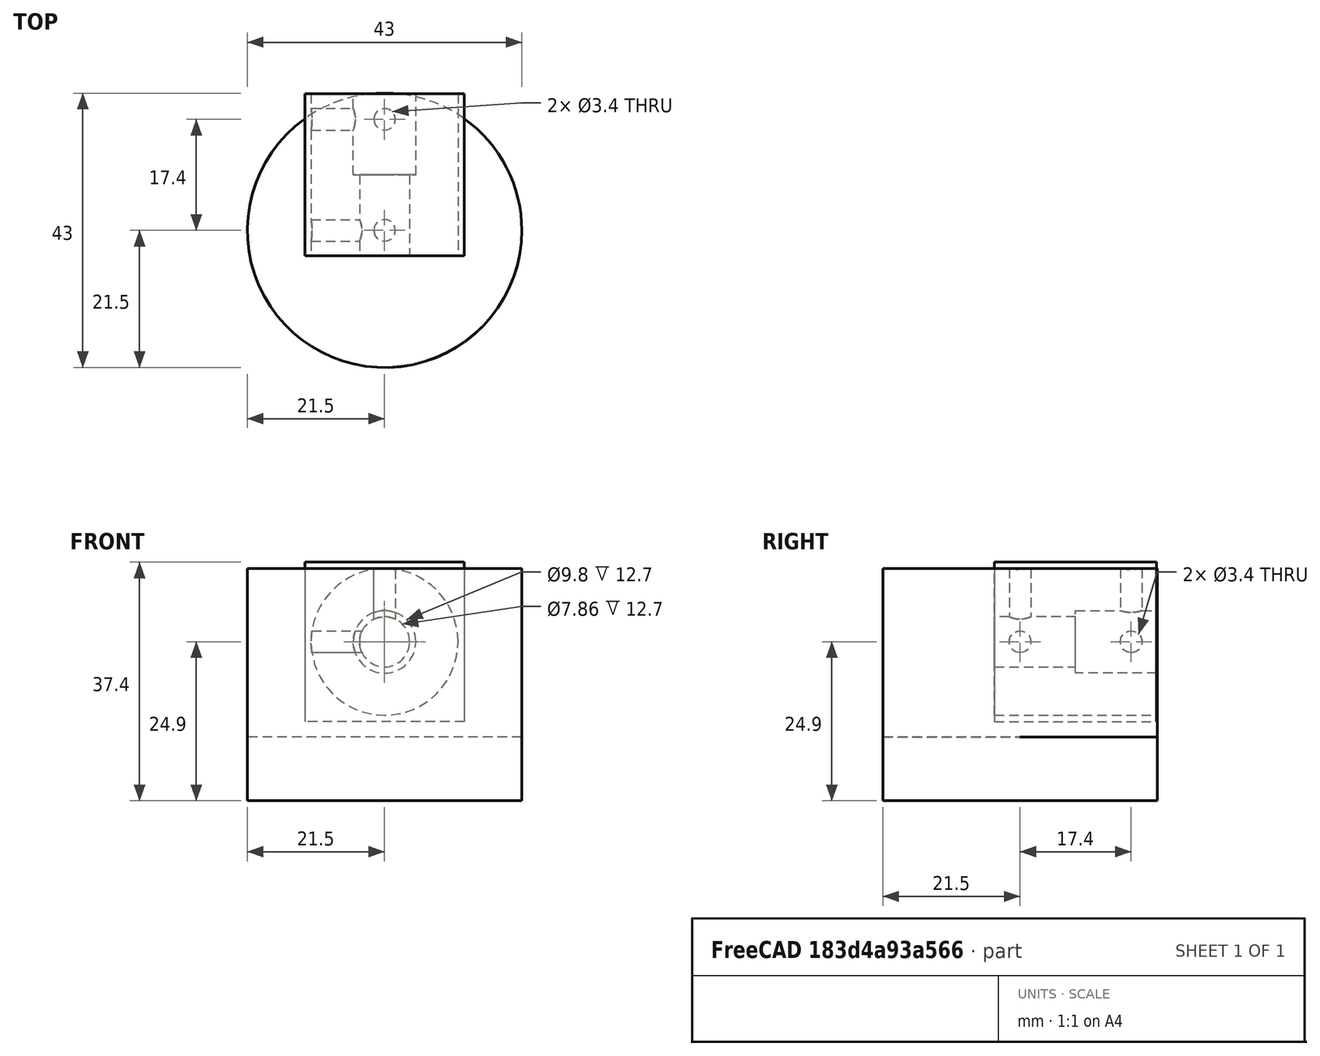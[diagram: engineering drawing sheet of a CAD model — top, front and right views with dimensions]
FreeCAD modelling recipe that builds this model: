
FCSTD DOCUMENT  (FreeCAD 0.17R13320 (Git))
Label: motor_coupler
License: All rights reserved
LicenseURL: http://en.wikipedia.org/wiki/All_rights_reserved
objects: Path::FeaturePython×15, Part::FeaturePython×6, Sketcher::SketchObject×4, PartDesign::Pocket×3, App::FeaturePython×3, Path::FeatureCompoundPython×3, PartDesign::Pad×1, PartDesign::Body×1, Mesh::FeaturePython×1
note: 22 computed .brp shape members not serialized (recipe doc carries the construction recipe); baked Part::Feature solids carry a one-line shape summary decoded from their .brp

FEATURE [Sketcher::SketchObject] Sketch
  MapMode = 5
  Support = -> [XY_Plane]
  sketch-geometry (2):
    g0: Circle CenterX=0 CenterY=0 CenterZ=0 NormalX=0 NormalY=0 NormalZ=1 AngleXU=0 Radius=11.5
    g1: Circle CenterX=0 CenterY=0 CenterZ=0 NormalX=0 NormalY=0 NormalZ=1 AngleXU=0 Radius=3.93
  constraints (4):
    c: Coincident(g0,g-1)
    c: Coincident(g1,g-1)
    c: Radius(g0) = 11.5
    c: Radius(g1) = 3.93
FEATURE [PartDesign::Pad] Pad
  Length = 25.4
  Length2 = 100
  Profile = -> Sketch
  Type = 0
FEATURE [Sketcher::SketchObject] Sketch001
  MapMode = 5
  Placement = pos=(0,0,25.4) rot=(0,0,1;0rad)
  Support = -> [Pad]
  sketch-geometry (1):
    g0: Circle CenterX=0 CenterY=0 CenterZ=0 NormalX=0 NormalY=0 NormalZ=1 AngleXU=0 Radius=4.9
  constraints (2):
    c: Radius(g0) = 4.9
    c: Coincident(g0,g-1)
FEATURE [PartDesign::Pocket] Pocket
  BaseFeature = -> Pad
  Length = 12.7
  Length2 = 100
  Profile = -> Sketch001
  Type = 0
FEATURE [Sketcher::SketchObject] Sketch002
  MapMode = 5
  Placement = pos=(0,0,0) rot=(1,0,0;1.5708rad)
  Support = -> [XZ_Plane]
  sketch-geometry (2):
    g0: Circle CenterX=0 CenterY=4 CenterZ=0 NormalX=0 NormalY=0 NormalZ=1 AngleXU=0 Radius=1.7
    g1: Circle CenterX=0 CenterY=21.4 CenterZ=0 NormalX=0 NormalY=0 NormalZ=1 AngleXU=0 Radius=1.7
  constraints (6):
    c: DistanceX(g-1,g0) = 0
    c: DistanceX(g-1,g1) = 0
    c: DistanceY(g-1,g0) = 4
    c: DistanceY(g-1,g1) = 21.4
    c: Radius(g0) = 1.7
    c: Equal(g1,g0)
FEATURE [PartDesign::Pocket] Pocket001
  BaseFeature = -> Pocket
  Length = 5
  Length2 = 100
  Profile = -> Sketch002
  Type = 1
FEATURE [Sketcher::SketchObject] Sketch003
  MapMode = 5
  Placement = pos=(0,0,0) rot=(0.57735,0.57735,0.57735;2.0944rad)
  Support = -> [YZ_Plane]
  sketch-geometry (2):
    g0: Circle CenterX=0 CenterY=4 CenterZ=0 NormalX=0 NormalY=0 NormalZ=1 AngleXU=0 Radius=1.7
    g1: Circle CenterX=0 CenterY=21.4 CenterZ=0 NormalX=0 NormalY=0 NormalZ=1 AngleXU=0 Radius=1.7
  constraints (6):
    c: PointOnObject(g0,g-2)
    c: PointOnObject(g1,g-2)
    c: DistanceY(g-1,g0) = 4
    c: DistanceY(g-1,g1) = 21.4
    c: Radius(g0) = 1.7
    c: Equal(g0,g1)
FEATURE [PartDesign::Pocket] Pocket002
  BaseFeature = -> Pocket001
  Length = 5
  Length2 = 100
  Profile = -> Sketch003
  Type = 1
FEATURE [PartDesign::Body] Body
  Group = -> [Sketch,Pad,Sketch001,Pocket,Sketch002,Pocket001,Sketch003,Pocket002]
  Origin = -> Origin
  Tip = -> Pocket002
FEATURE [App::FeaturePython] SetupSheet  # Path/CAM operation (typed FeaturePython)
  ClearanceHeightExpression = StartDepth+SetupSheet.ClearanceHeightOffset
  ClearanceHeightOffset = 5
  FinalDepthExpression = OpFinalDepth
  HorizRapid = 0
  SafeHeightExpression = StartDepth+SetupSheet.SafeHeightOffset
  SafeHeightOffset = 3
  StartDepthExpression = OpStartDepth
  StepDownExpression = OpToolDiameter
  VertRapid = 0
FEATURE [Part::FeaturePython] Clone  label="Base-Body"  # Draft clone (typed FeaturePython)
  AttacherType = Attacher::AttachEngine3D
  Fuse = false
  Objects = -> [Body]
  PathResource = Base
  Placement = pos=(0,0,-26.4) rot=(0,0,1;0rad)
  Scale = (1,1,1)
FEATURE [Path::FeaturePython] Default_Tool  label="Default Tool"  # Path/CAM operation (typed FeaturePython)
  HorizFeed = 0
  HorizRapid = 0
  SpindleDir = 0
  SpindleSpeed = 0
  ToolNumber = 1
  VertFeed = 0
  VertRapid = 0
  expr: HorizRapid = SetupSheet.HorizRapid
  expr: VertRapid = SetupSheet.VertRapid
FEATURE [Part::FeaturePython] Stock001  # WARN: FeaturePython — macro-defined, semantics opaque (R4)
  Height = 26.4
  Placement = pos=(0,0.0031811,-26.4) rot=(0,0,1;0rad)
  Radius = 21.5
  StockType = CreateCylinder
FEATURE [Path::FeaturePython] T3__8mm  label="T3: 8mm"  # Path/CAM operation (typed FeaturePython)
  HorizFeed = 0
  HorizRapid = 0
  SpindleDir = 0
  SpindleSpeed = 0
  ToolNumber = 3
  VertFeed = 0
  VertRapid = 0
  expr: HorizRapid = SetupSheet.HorizRapid
  expr: VertRapid = SetupSheet.VertRapid
FEATURE [Path::FeaturePython] MillFace  # Path/CAM operation (typed FeaturePython)
  Active = true
  AreaParams:
    OpenMode = 0
    Angle = 45.0
    MinArcPoints = 4
    Coplanar = 0
    Tolerance = 1e-07
    CleanDistance = 0.0
    PocketExtraOffset = -1.0
    RoundPrecision = 0.0
    AngleShift = 0.0
    SubjectFill = 0
    PocketMode = 2
    Simplify = False
    SectionTolerance = 1e-06
    MaxArcPoints = 100
    Offset = 0.0
    Accuracy = 0.01
    PocketStepover = 3.2
    ClipFill = 0
    ToolRadius = 4.0
    Outline = False
    ClipperScale = 10000000.0
    FromCenter = True
    Explode = False
    EndType = 0
    Shift = 0.0
    ExtraPass = 0
    Project = False
    JoinType = 0
    Thicken = False
    Stepdown = 1.0
    SectionMode = 2
    MiterLimit = 2.0
    Deflection = 0.01
    Reorient = True
    FitArcs = True
    SectionCount = -1
    SectionOffset = 0.0
    Stepover = 0.0
    Unit = 1.0
    Fill = 0
  Base = -> [Clone]
  BoundaryShape = 0
  ClearanceHeight = 5
  CutMode = 0
  ExtraOffset = 1
  FinalDepth = -1
  FinishDepth = 0
  KeepToolDown = false
  MinTravel = false
  OffsetPattern = 1
  OpFinalDepth = -1
  OpStartDepth = 0
  OpToolDiameter = 8
  PathParams = {'resume_height': 3.0, 'feedrate': 0.0, 'verbose': True, 'orientation': 1, 'return_end': True, 'preamble': False, 'retraction': 5.0, 'feedrate_v': 0.0}
  SafeHeight = 3
  StartAt = 0
  StartDepth = 0
  StartPoint = (0,0,0)
  StepDown = 0.5
  StepOver = 40
  ToolController = -> T3__8mm
  UseStartPoint = false
  ZigZagAngle = 45
  expr: ClearanceHeight = StartDepth + SetupSheet.ClearanceHeightOffset
  expr: SafeHeight = StartDepth + SetupSheet.SafeHeightOffset
  expr: FinalDepth = OpFinalDepth
  expr: StartDepth = OpStartDepth
FEATURE [Path::FeaturePython] Helix  # Path/CAM operation (typed FeaturePython)
  Active = true
  Base = -> [Clone]
  ClearanceHeight = 5
  Direction = 0
  FinalDepth = -13.7
  OpFinalDepth = -13.7
  OpStartDepth = 0
  OpToolDiameter = 8
  SafeHeight = 3
  StartDepth = 0
  StartSide = 0
  StepDown = 0.5
  StepOver = 90
  ToolController = -> T3__8mm
  expr: ClearanceHeight = StartDepth + SetupSheet.ClearanceHeightOffset
  expr: SafeHeight = StartDepth + SetupSheet.SafeHeightOffset
  expr: FinalDepth = OpFinalDepth
  expr: StartDepth = OpStartDepth
FEATURE [Path::FeaturePython] Helix001  # Path/CAM operation (typed FeaturePython)
  Active = true
  Base = -> [Clone]
  ClearanceHeight = 5
  Direction = 0
  FinalDepth = -26.4
  OpFinalDepth = -26.4
  OpStartDepth = 0
  OpToolDiameter = 8
  SafeHeight = 3
  StartDepth = 0
  StartSide = 0
  StepDown = 1
  StepOver = 30
  ToolController = -> T3__8mm
  expr: ClearanceHeight = StartDepth + SetupSheet.ClearanceHeightOffset
  expr: SafeHeight = StartDepth + SetupSheet.SafeHeightOffset
  expr: FinalDepth = OpFinalDepth
  expr: StartDepth = OpStartDepth
FEATURE [Path::FeaturePython] Contour  # Path/CAM operation (typed FeaturePython)
  Active = true
  AreaParams:
    OpenMode = 0
    Angle = 45.0
    MinArcPoints = 4
    Coplanar = 2
    Tolerance = 1e-07
    CleanDistance = 0.0
    PocketExtraOffset = 0.0
    RoundPrecision = 0.0
    AngleShift = 0.0
    SubjectFill = 0
    PocketMode = 0
    Simplify = False
    SectionTolerance = 1e-06
    MaxArcPoints = 100
    Offset = 4.0
    Accuracy = 0.01
    PocketStepover = 0.0
    ClipFill = 0
    ToolRadius = 1.0
    Outline = False
    ClipperScale = 10000000.0
    FromCenter = False
    Explode = False
    EndType = 0
    Shift = 0.0
    ExtraPass = 0
    Project = False
    JoinType = 0
    Thicken = False
    Stepdown = 1.0
    SectionMode = 2
    MiterLimit = 2.0
    Deflection = 0.01
    Reorient = True
    FitArcs = True
    SectionCount = -1
    SectionOffset = 0.0
    Stepover = 0.0
    Unit = 1.0
    Fill = 0
  ClearanceHeight = 5
  Direction = 1
  FinalDepth = -26.4
  JoinType = 0
  MiterLimit = 0.1
  OffsetExtra = 0
  OpFinalDepth = -26.4
  OpStartDepth = 0
  OpToolDiameter = 8
  PathParams = {'resume_height': 3.0, 'feedrate': 0.0, 'verbose': True, 'orientation': 0, 'return_end': True, 'preamble': False, 'retraction': 5.0, 'feedrate_v': 0.0}
  SafeHeight = 3
  Side = 0
  StartDepth = 0
  StartPoint = (0,0,0)
  StepDown = 0.5
  ToolController = -> T3__8mm
  UseComp = true
  UseStartPoint = false
  expr: ClearanceHeight = StartDepth + SetupSheet.ClearanceHeightOffset
  expr: SafeHeight = StartDepth + SetupSheet.SafeHeightOffset
  expr: StartDepth = OpStartDepth
FEATURE [Path::FeatureCompoundPython] Operations  # Path/CAM operation (typed FeaturePython)
  Group = -> [MillFace,Helix,Helix001,Contour]
  UsePlacements = false
FEATURE [Path::FeaturePython] Job  # Path/CAM operation (typed FeaturePython)
  Base = -> Clone
  GeometryTolerance = 0.01
  Operations = -> Operations
  PostProcessor = 5
  SetupSheet = -> SetupSheet
  Stock = -> Stock001
  ToolController = -> [Default_Tool,T3__8mm]
FEATURE [Mesh::FeaturePython] CutMaterial  # WARN: FeaturePython — macro-defined, semantics opaque (R4)
FEATURE [App::FeaturePython] SetupSheet001  # Path/CAM operation (typed FeaturePython)
  ClearanceHeightExpression = StartDepth+SetupSheet001.ClearanceHeightOffset
  ClearanceHeightOffset = 5
  FinalDepthExpression = OpFinalDepth
  HorizRapid = 0
  SafeHeightExpression = StartDepth+SetupSheet001.SafeHeightOffset
  SafeHeightOffset = 3
  StartDepthExpression = OpStartDepth
  StepDownExpression = OpToolDiameter
  VertRapid = 0
FEATURE [Part::FeaturePython] Clone001  label="Base-Body001"  # Draft clone (typed FeaturePython)
  AttacherType = Attacher::AttachEngine3D
  Fuse = false
  Objects = -> [Body]
  PathResource = Base
  Placement = pos=(0,0,-11) rot=(1,0,0;3.14159rad)
  Scale = (1,1,1)
FEATURE [Path::FeaturePython] Default_Tool001  label="Default Tool001"  # Path/CAM operation (typed FeaturePython)
  HorizFeed = 0
  HorizRapid = 0
  SpindleDir = 0
  SpindleSpeed = 0
  ToolNumber = 1
  VertFeed = 0
  VertRapid = 0
  expr: HorizRapid = SetupSheet001.HorizRapid
  expr: VertRapid = SetupSheet001.VertRapid
FEATURE [App::FeaturePython] SetupSheet002  # Path/CAM operation (typed FeaturePython)
  ClearanceHeightExpression = StartDepth+SetupSheet002.ClearanceHeightOffset
  ClearanceHeightOffset = 5
  FinalDepthExpression = OpFinalDepth
  HorizRapid = 0
  SafeHeightExpression = StartDepth+SetupSheet002.SafeHeightOffset
  SafeHeightOffset = 3
  StartDepthExpression = OpStartDepth
  StepDownExpression = OpToolDiameter
  VertRapid = 0
FEATURE [Part::FeaturePython] Clone002  label="Base-Body002"  # Draft clone (typed FeaturePython)
  AttacherType = Attacher::AttachEngine3D
  Fuse = false
  Objects = -> [Body]
  PathResource = Base
  Placement = pos=(0,-4,-11.5) rot=(0.57735,-0.57735,-0.57735;4.18879rad)
  Scale = (1,1,1)
FEATURE [Path::FeaturePython] Default_Tool002  label="Default Tool002"  # Path/CAM operation (typed FeaturePython)
  HorizFeed = 0
  HorizRapid = 0
  SpindleDir = 0
  SpindleSpeed = 0
  ToolNumber = 1
  VertFeed = 0
  VertRapid = 0
  expr: HorizRapid = SetupSheet002.HorizRapid
  expr: VertRapid = SetupSheet002.VertRapid
FEATURE [Part::FeaturePython] Stock  # WARN: FeaturePython — macro-defined, semantics opaque (R4)
  Base = -> Body
  ExtXneg = 1
  ExtXpos = 1
  ExtYneg = 1
  ExtYpos = 1
  ExtZneg = 0
  ExtZpos = 0
  Placement = pos=(0,-4,-11.5) rot=(-0.57735,0.57735,0.57735;2.0944rad)
  StockType = FromBase
FEATURE [Path::FeaturePython] T8__3mm  label="T8: 3mm"  # Path/CAM operation (typed FeaturePython)
  HorizFeed = 0
  HorizRapid = 0
  SpindleDir = 0
  SpindleSpeed = 0
  ToolNumber = 8
  VertFeed = 0
  VertRapid = 0
  expr: HorizRapid = SetupSheet002.HorizRapid
  expr: VertRapid = SetupSheet002.VertRapid
FEATURE [Path::FeaturePython] Helix002  # Path/CAM operation (typed FeaturePython)
  Active = true
  Base = -> [Clone002]
  ClearanceHeight = 6
  Direction = 0
  FinalDepth = -7.71
  OpFinalDepth = -6.91251
  OpStartDepth = 1
  OpToolDiameter = 3
  SafeHeight = 4
  StartDepth = 1
  StartSide = 0
  StepDown = 0.5
  StepOver = 40
  ToolController = -> T8__3mm
  expr: ClearanceHeight = StartDepth + SetupSheet002.ClearanceHeightOffset
  expr: SafeHeight = StartDepth + SetupSheet002.SafeHeightOffset
  expr: StartDepth = OpStartDepth
FEATURE [Path::FeatureCompoundPython] Operations002  # Path/CAM operation (typed FeaturePython)
  Group = -> [Helix002]
  UsePlacements = false
FEATURE [Path::FeaturePython] Job002  # Path/CAM operation (typed FeaturePython)
  Base = -> Clone002
  GeometryTolerance = 0.01
  Operations = -> Operations002
  PostProcessor = 5
  SetupSheet = -> SetupSheet002
  Stock = -> Stock
  ToolController = -> [Default_Tool002,T8__3mm]
FEATURE [Path::FeaturePython] T3__8mm001  label="T3: 8mm001"  # Path/CAM operation (typed FeaturePython)
  HorizFeed = 0
  HorizRapid = 0
  SpindleDir = 0
  SpindleSpeed = 0
  ToolNumber = 3
  VertFeed = 0
  VertRapid = 0
  expr: HorizRapid = SetupSheet001.HorizRapid
  expr: VertRapid = SetupSheet001.VertRapid
FEATURE [Path::FeaturePython] MillFace001  # Path/CAM operation (typed FeaturePython)
  Active = true
  AreaParams:
    OpenMode = 0
    Angle = 45.0
    MinArcPoints = 4
    Coplanar = 0
    Tolerance = 1e-07
    CleanDistance = 0.0
    PocketExtraOffset = 2.0
    RoundPrecision = 0.0
    AngleShift = 0.0
    SubjectFill = 0
    PocketMode = 2
    Simplify = False
    SectionTolerance = 1e-06
    MaxArcPoints = 100
    Offset = 0.0
    Accuracy = 0.01
    PocketStepover = 3.2
    ClipFill = 0
    ToolRadius = 4.0
    Outline = False
    ClipperScale = 10000000.0
    FromCenter = True
    Explode = False
    EndType = 0
    Shift = 0.0
    ExtraPass = 0
    Project = False
    JoinType = 0
    Thicken = False
    Stepdown = 1.0
    SectionMode = 2
    MiterLimit = 2.0
    Deflection = 0.01
    Reorient = True
    FitArcs = True
    SectionCount = -1
    SectionOffset = 0.0
    Stepover = 0.0
    Unit = 1.0
    Fill = 0
  Base = -> [Clone001]
  BoundaryShape = 2
  ClearanceHeight = 5
  CutMode = 0
  ExtraOffset = -2
  FinalDepth = -11
  FinishDepth = 0
  KeepToolDown = false
  MinTravel = false
  OffsetPattern = 1
  OpFinalDepth = -11
  OpStartDepth = 0
  OpToolDiameter = 8
  PathParams = {'resume_height': 3.0, 'feedrate': 0.0, 'verbose': True, 'orientation': 1, 'return_end': True, 'preamble': False, 'retraction': 5.0, 'feedrate_v': 0.0}
  SafeHeight = 3
  StartAt = 0
  StartDepth = 0
  StartPoint = (0,0,0)
  StepDown = 0.5
  StepOver = 40
  ToolController = -> T3__8mm001
  UseStartPoint = false
  ZigZagAngle = 45
  expr: ClearanceHeight = StartDepth + SetupSheet001.ClearanceHeightOffset
  expr: SafeHeight = StartDepth + SetupSheet001.SafeHeightOffset
  expr: FinalDepth = OpFinalDepth
  expr: StartDepth = OpStartDepth
FEATURE [Path::FeatureCompoundPython] Operations001  # Path/CAM operation (typed FeaturePython)
  Group = -> [MillFace001]
  UsePlacements = false
FEATURE [Part::FeaturePython] Stock004  # WARN: FeaturePython — macro-defined, semantics opaque (R4)
  Height = 36.4
  Placement = pos=(0,-0.0031811,-36.4) rot=(0,0,1;0rad)
  Radius = 21.5
  StockType = CreateCylinder
FEATURE [Path::FeaturePython] Job001  # Path/CAM operation (typed FeaturePython)
  Base = -> Clone001
  GeometryTolerance = 0.01
  Operations = -> Operations001
  PostProcessor = 5
  SetupSheet = -> SetupSheet001
  Stock = -> Stock004
  ToolController = -> [Default_Tool001,T3__8mm001]
